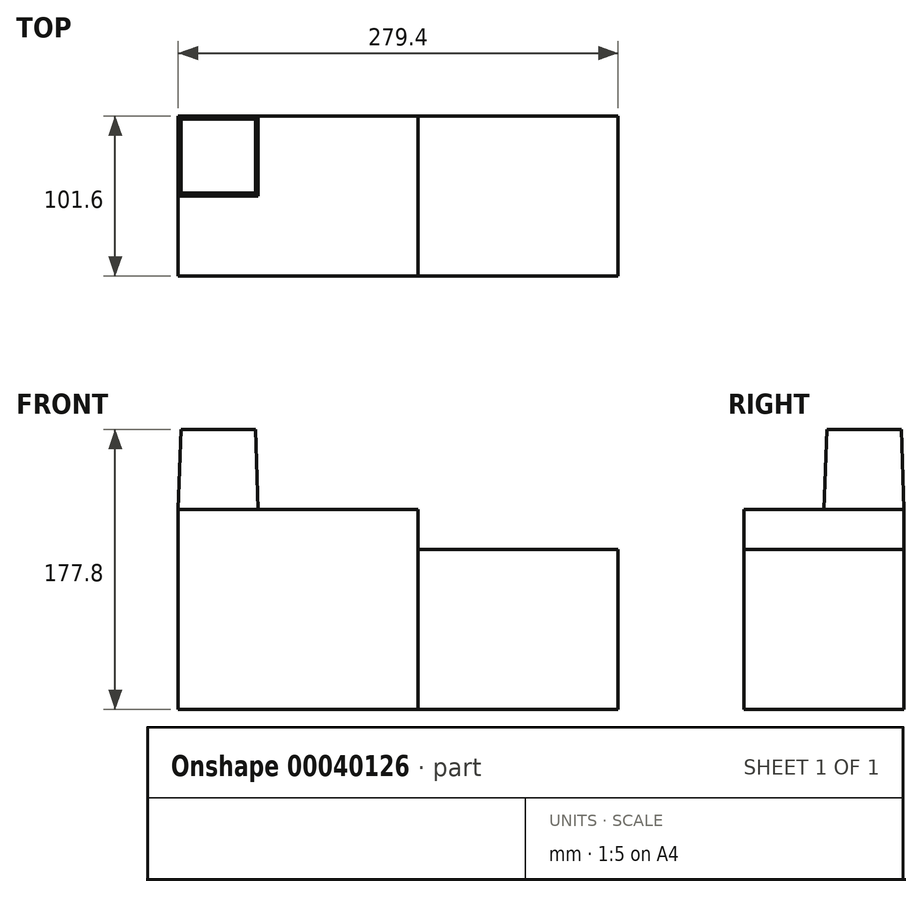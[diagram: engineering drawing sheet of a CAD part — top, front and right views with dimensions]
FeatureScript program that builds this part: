
annotation { "Feature Type Name" : "Feature", "Feature Type Description" : "" }
export const myFeature = defineFeature(function(context is Context, id is Id, definition is map)
    precondition{}
    {
        {
            var Q0;
            Q0=qCreatedBy(makeId("Top.planeOp"),FACE);
            var sketch = newSketch(context, id + "F0", { "sketchPlane" : qUnion([Q0])});
            skLineSegment(sketch, "E0.bottom", {"start": v(0, 0) * mm, "end": v(-152.4, 0) * mm});
            skLineSegment(sketch, "E0.top", {"start": v(0, -101.6) * mm, "end": v(-152.4, -101.6) * mm});
            skLineSegment(sketch, "E0.left", {"start": v(0, 0) * mm, "end": v(0, -101.6) * mm});
            skLineSegment(sketch, "E0.right", {"start": v(-152.4, 0) * mm, "end": v(-152.4, -101.6) * mm});
            skLineSegment(sketch, "E1.top", {"start": v(-152.4, -101.6) * mm, "end": v(-73.88, -101.6) * mm});
            skLineSegment(sketch, "E1.left", {"start": v(-152.4, -83.5) * mm, "end": v(-152.4, -101.6) * mm});
            skSolve(sketch);
        }
        {
            var Q0;
            Q0=makeQuery(id+"F0.imprint","IMPRINT",FACE,{"disambiguationData":[TD([[makeQuery(id+"F0.imprint","IMPRINT",EDGE,{"derivedFrom":sQuery(id+"F0.wireOp",EDGE,"E0.bottom")}),1.0]])]});
            extrude(context, id + "F1", {"entities" : qUnion([Q0]), "depth" : 127 * mm});
        }
        {
            var Q0;
            Q0=makeQuery(id+"F1.opExtrude","CAP_FACE",FACE,{"disambiguationData":[OSD([sQuery(id+"F0.wireOp",EDGE,"E0.bottom"),sQuery(id+"F0.wireOp",EDGE,"E0.top"),sQuery(id+"F0.wireOp",EDGE,"E0.left"),sQuery(id+"F0.wireOp",EDGE,"E0.right"),sQuery(id+"F0.wireOp",EDGE,"E1.top"),sQuery(id+"F0.wireOp",EDGE,"E1.left")])],"isStart":false});
            var sketch = newSketch(context, id + "F2", { "sketchPlane" : qUnion([Q0])});
            skLineSegment(sketch, "E2.bottom", {"start": v(-152.4, 0) * mm, "end": v(-101.6, 0) * mm});
            skLineSegment(sketch, "E2.top", {"start": v(-152.4, -50.8) * mm, "end": v(-101.6, -50.8) * mm});
            skLineSegment(sketch, "E2.left", {"start": v(-152.4, 0) * mm, "end": v(-152.4, -50.8) * mm});
            skLineSegment(sketch, "E2.right", {"start": v(-101.6, 0) * mm, "end": v(-101.6, -50.8) * mm});
            skSolve(sketch);
        }
        {
            var Q0;
            Q0=makeQuery(id+"F2.imprint","IMPRINT",FACE,{"disambiguationData":[TD([[makeQuery(id+"F2.imprint","IMPRINT",EDGE,{"derivedFrom":sQuery(id+"F2.wireOp",EDGE,"E2.bottom")}),1.0]])]});
            extrude(context, id + "F3", {"entities" : qUnion([Q0]), "operationType" : NewBodyOperationType.ADD, "depth" : 50.8 * mm, "hasDraft" : true, "draftAngle" : 2 * degree, "draftPullDirection" : true});
        }
        {
            var Q0;
            Q0=makeQuery(id+"F1.opExtrude","SWEPT_FACE",FACE,{"disambiguationData":[OSD([sQuery(id+"F0.wireOp",EDGE,"E0.left")])]});
            var sketch = newSketch(context, id + "F4", { "sketchPlane" : qUnion([Q0])});
            skLineSegment(sketch, "E3.bottom", {"start": v(0, 0) * mm, "end": v(-101.6, 0) * mm});
            skLineSegment(sketch, "E3.top", {"start": v(0, 101.6) * mm, "end": v(-101.6, 101.6) * mm});
            skLineSegment(sketch, "E3.left", {"start": v(0, 0) * mm, "end": v(0, 101.6) * mm});
            skLineSegment(sketch, "E3.right", {"start": v(-101.6, 0) * mm, "end": v(-101.6, 101.6) * mm});
            skSolve(sketch);
        }
        {
            var Q0;
            Q0=makeQuery(id+"F4.imprint","IMPRINT",FACE,{"disambiguationData":[TD([[makeQuery(id+"F4.imprint","IMPRINT",EDGE,{"derivedFrom":sQuery(id+"F4.wireOp",EDGE,"E3.bottom")}),-1.0]])]});
            extrude(context, id + "F5", {"entities" : qUnion([Q0]), "depth" : 127 * mm});
        }
    });
